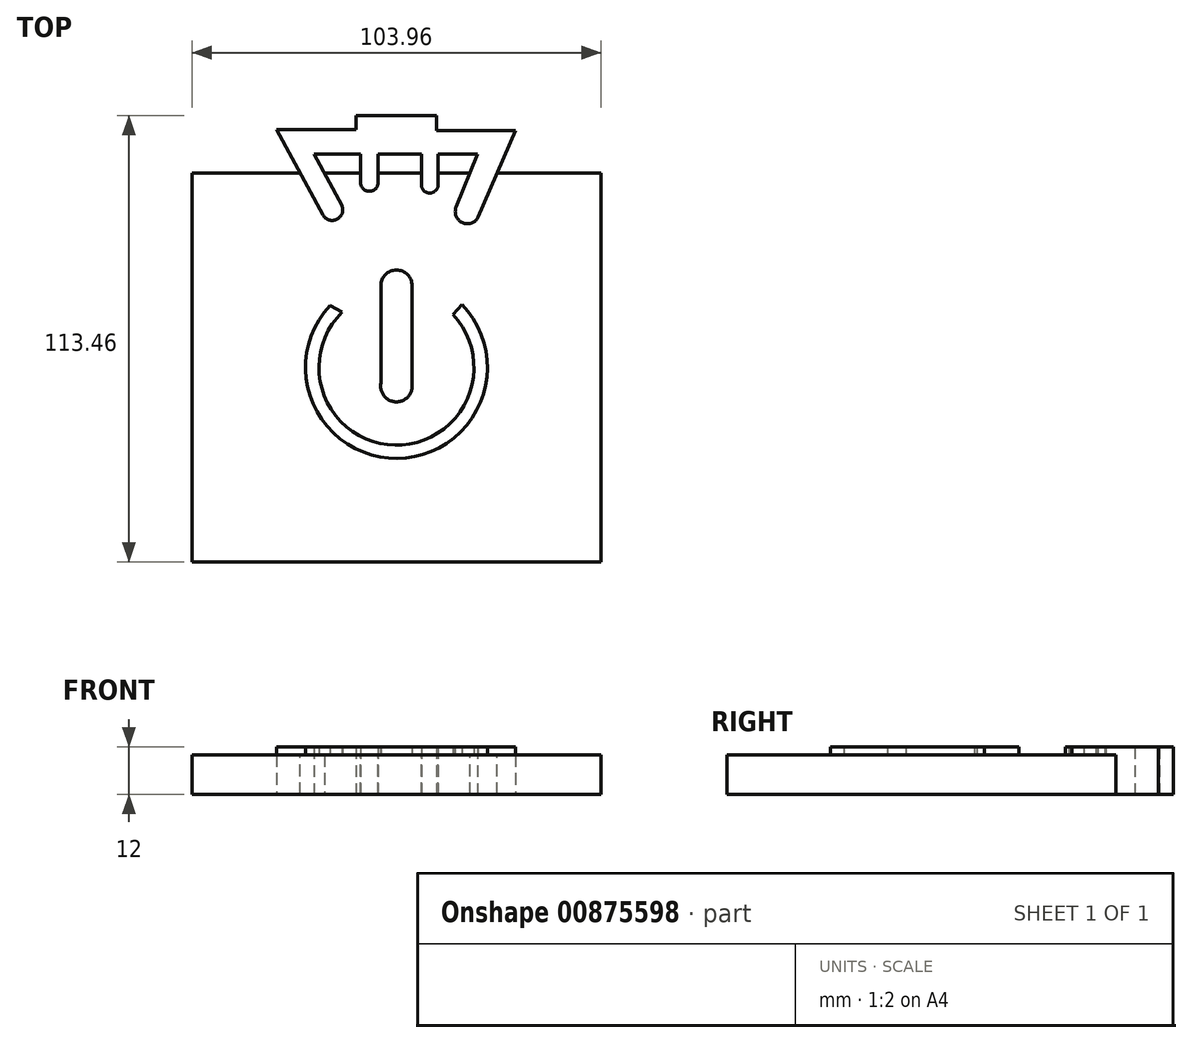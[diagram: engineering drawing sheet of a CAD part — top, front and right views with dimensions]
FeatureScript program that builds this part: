
annotation { "Feature Type Name" : "Feature", "Feature Type Description" : "" }
export const myFeature = defineFeature(function(context is Context, id is Id, definition is map)
    precondition{}
    {
        {
            var Q0;
            Q0=qCreatedBy(makeId("Top.planeOp"),FACE);
            var sketch = newSketch(context, id + "F0", { "sketchPlane" : qUnion([Q0])});
            skLineSegment(sketch, "E0.bottom", {"start": v(51.98, 49.43) * mm, "end": v(-51.98, 49.43) * mm});
            skLineSegment(sketch, "E0.top", {"start": v(51.98, -49.43) * mm, "end": v(-51.98, -49.43) * mm});
            skLineSegment(sketch, "E0.left", {"start": v(51.98, 49.43) * mm, "end": v(51.98, -49.43) * mm});
            skLineSegment(sketch, "E0.right", {"start": v(-51.98, 49.43) * mm, "end": v(-51.98, -49.43) * mm});
            skPoint(sketch, "E0.middle", {"position": v(0, 0) * mm});
            skSolve(sketch);
        }
        {
            var Q0;
            Q0 = qSketchRegion(id + "F0", true);
            extrude(context, id + "F1", {"entities" : qUnion([Q0]), "depth" : 10 * mm, "offsetDistance" : 25 * mm});
        }
        {
            var Q0;
            Q0=makeQuery(id+"F1.opExtrude","CAP_FACE",FACE,{"disambiguationData":[OSD([sQuery(id+"F0.wireOp",EDGE,"E0.bottom"),sQuery(id+"F0.wireOp",EDGE,"E0.top"),sQuery(id+"F0.wireOp",EDGE,"E0.left"),sQuery(id+"F0.wireOp",EDGE,"E0.right")])],"isStart":false});
            var sketch = newSketch(context, id + "F2", { "sketchPlane" : qUnion([Q0])});
            skArc(sketch, "E1", {"start": v(0, -23.09) * mm, "mid": v(21.25, -9.03) * mm, "end": v(16.62, 16.02) * mm});
            skArc(sketch, "E2", {"start": v(0, -23.09) * mm, "mid": v(-21.17, -9.21) * mm, "end": v(-16.9, 15.74) * mm});
            skArc(sketch, "E3", {"start": v(0, -19.69) * mm, "mid": v(18.07, -7.81) * mm, "end": v(14.34, 13.49) * mm});
            skArc(sketch, "E4", {"start": v(0, -19.69) * mm, "mid": v(-18.23, -7.44) * mm, "end": v(-13.78, 14.06) * mm});
            skLineSegment(sketch, "E5", {"start": v(-16.9, 15.74) * mm, "end": v(-13.78, 14.06) * mm});
            skLineSegment(sketch, "E6", {"start": v(16.62, 16.02) * mm, "end": v(14.34, 13.49) * mm});
            skSolve(sketch);
        }
        {
            var Q0;
            Q0 = qSketchRegion(id + "F2", true);
            extrude(context, id + "F3", {"entities" : qUnion([Q0]), "operationType" : NewBodyOperationType.ADD, "depth" : 2 * mm, "offsetDistance" : 25 * mm});
        }
        {
            var Q0;
            Q0=makeQuery(id+"F1.opExtrude","CAP_FACE",FACE,{"disambiguationData":[OSD([sQuery(id+"F0.wireOp",EDGE,"E0.bottom"),sQuery(id+"F0.wireOp",EDGE,"E0.top"),sQuery(id+"F0.wireOp",EDGE,"E0.left"),sQuery(id+"F0.wireOp",EDGE,"E0.right")])],"isStart":false});
            var sketch = newSketch(context, id + "F4", { "sketchPlane" : qUnion([Q0])});
            skArc(sketch, "E7", {"start": v(0, -8.7) * mm, "mid": v(3.1, -7.26) * mm, "end": v(3.97, -3.95) * mm});
            skArc(sketch, "E8", {"start": v(0, -8.7) * mm, "mid": v(-3.1, -7.26) * mm, "end": v(-3.97, -3.95) * mm});
            skLineSegment(sketch, "E9", {"start": v(-3.97, -3.95) * mm, "end": v(-3.97, 20.82) * mm});
            skLineSegment(sketch, "E10", {"start": v(3.97, -3.95) * mm, "end": v(3.97, 20.82) * mm});
            skArc(sketch, "E11", {"start": v(0, 24.79) * mm, "mid": v(-2.8, 23.62) * mm, "end": v(-3.97, 20.82) * mm});
            skArc(sketch, "E12", {"start": v(0, 24.79) * mm, "mid": v(2.8, 23.62) * mm, "end": v(3.97, 20.82) * mm});
            skPoint(sketch, "E13.orphan", {"position": v(-3.97, 20.82) * mm});
            skSolve(sketch);
        }
        {
            var Q0;
            Q0=makeQuery(id+"F4.imprint","IMPRINT",FACE,{"disambiguationData":[TD([[makeQuery(id+"F4.imprint","IMPRINT",EDGE,{"derivedFrom":sQuery(id+"F4.wireOp",EDGE,"E7")}),1.0]])]});
            extrude(context, id + "F5", {"entities" : qUnion([Q0]), "operationType" : NewBodyOperationType.ADD, "depth" : 2 * mm, "offsetDistance" : 25 * mm});
        }
        {
            var Q0;
            Q0=qCreatedBy(makeId("Top.planeOp"),FACE);
            var sketch = newSketch(context, id + "F6", { "sketchPlane" : qUnion([Q0])});
            skLineSegment(sketch, "E14", {"start": v(0, 64.03) * mm, "end": v(10.16, 64.03) * mm});
            skLineSegment(sketch, "E15", {"start": v(10.16, 64.03) * mm, "end": v(10.16, 60.23) * mm});
            skLineSegment(sketch, "E16", {"start": v(10.16, 60.23) * mm, "end": v(30.2, 60.23) * mm});
            skLineSegment(sketch, "E17", {"start": v(30.2, 60.23) * mm, "end": v(20.78, 38.2) * mm});
            skLineSegment(sketch, "E18", {"start": v(0, 64.03) * mm, "end": v(-10.27, 64.03) * mm});
            skLineSegment(sketch, "E19", {"start": v(-10.27, 64.03) * mm, "end": v(-10.27, 60.43) * mm});
            skLineSegment(sketch, "E20", {"start": v(-10.27, 60.43) * mm, "end": v(-30.5, 60.43) * mm});
            skLineSegment(sketch, "E21", {"start": v(-30.5, 60.43) * mm, "end": v(-18.68, 38.8) * mm});
            skLineSegment(sketch, "E22", {"start": v(-13.87, 41.2) * mm, "end": v(-20.88, 54.22) * mm});
            skLineSegment(sketch, "E23", {"start": v(-20.88, 54.22) * mm, "end": v(20.58, 54.22) * mm});
            skLineSegment(sketch, "E24", {"start": v(20.58, 54.22) * mm, "end": v(15.17, 40.8) * mm});
            skLineSegment(sketch, "E25", {"start": v(-9.07, 54.22) * mm, "end": v(-9.07, 46.6) * mm});
            skLineSegment(sketch, "E26", {"start": v(-4.66, 54.22) * mm, "end": v(-4.66, 47) * mm});
            skLineSegment(sketch, "E27", {"start": v(6.36, 54.22) * mm, "end": v(6.36, 46.8) * mm});
            skLineSegment(sketch, "E28", {"start": v(10.56, 54.22) * mm, "end": v(10.56, 46.8) * mm});
            skArc(sketch, "E29", {"start": v(-18.68, 38.8) * mm, "mid": v(-15.12, 37.68) * mm, "end": v(-13.87, 41.2) * mm});
            skArc(sketch, "E30", {"start": v(15.17, 40.8) * mm, "mid": v(16.74, 36.83) * mm, "end": v(20.78, 38.2) * mm});
            skArc(sketch, "E31", {"start": v(-9.07, 46.6) * mm, "mid": v(-6.68, 44.8) * mm, "end": v(-4.66, 47) * mm});
            skArc(sketch, "E32", {"start": v(6.36, 46.8) * mm, "mid": v(8.46, 44.34) * mm, "end": v(10.56, 46.8) * mm});
            skSolve(sketch);
        }
        {
            var Q0;
            Q0=makeQuery(id+"F6.imprint","IMPRINT",FACE,{"disambiguationData":[TD([[makeQuery(id+"F6.imprint","IMPRINT",EDGE,{"derivedFrom":sQuery(id+"F6.wireOp",EDGE,"E14")}),-1.0]])]});
            var Q1;
            {var subQ0=sQuery(id+"F6.wireOp",EDGE,"E27");Q1=makeQuery(id+"F6.imprint","IMPRINT",FACE,{"disambiguationData":[TD([[makeQuery(id+"F6.imprint","IMPRINT",EDGE,{"derivedFrom":subQ0}),1.0]])]});}
            var Q2;
            {var subQ0=sQuery(id+"F6.wireOp",EDGE,"E25");Q2=makeQuery(id+"F6.imprint","IMPRINT",FACE,{"disambiguationData":[TD([[makeQuery(id+"F6.imprint","IMPRINT",EDGE,{"derivedFrom":subQ0}),1.0]])]});}
            extrude(context, id + "F7", {"entities" : qUnion([Q0, Q1, Q2]), "operationType" : NewBodyOperationType.ADD, "depth" : 12 * mm, "offsetDistance" : 25 * mm});
        }
    });
